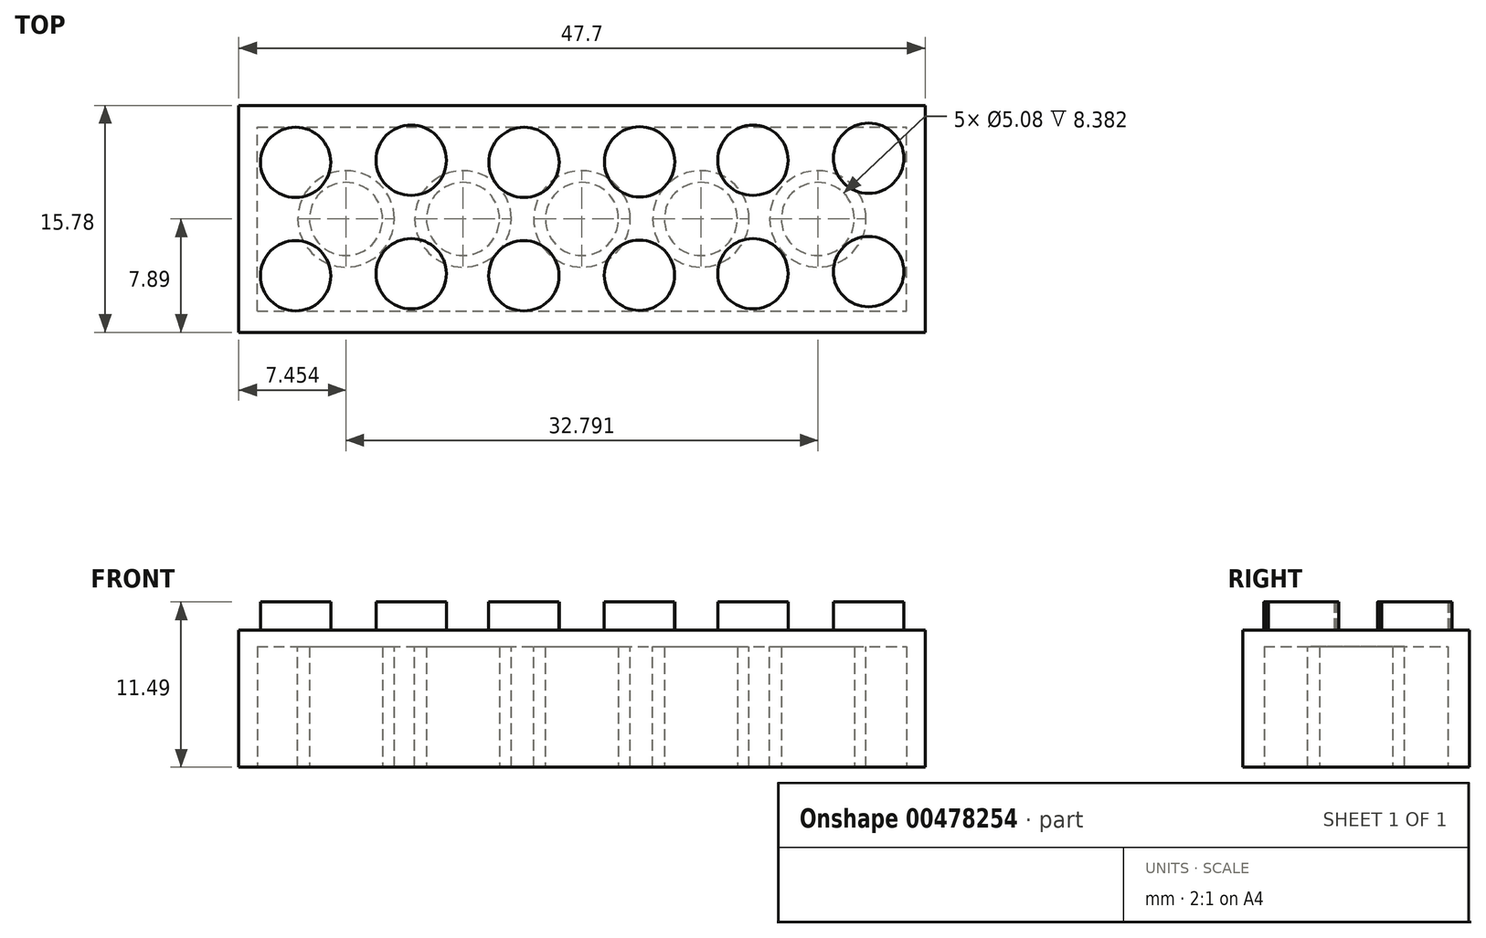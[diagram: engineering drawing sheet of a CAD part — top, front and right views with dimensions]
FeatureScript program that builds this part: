
annotation { "Feature Type Name" : "Feature", "Feature Type Description" : "" }
export const myFeature = defineFeature(function(context is Context, id is Id, definition is map)
    precondition{}
    {
        {
            var Q0;
            Q0=qCreatedBy(makeId("Top.planeOp"),FACE);
            var sketch = newSketch(context, id + "F0", { "sketchPlane" : qUnion([Q0])});
            skLineSegment(sketch, "E0.bottom", {"start": v(23.85, 7.89) * mm, "end": v(-23.85, 7.89) * mm});
            skLineSegment(sketch, "E0.top", {"start": v(23.85, -7.89) * mm, "end": v(-23.85, -7.89) * mm});
            skLineSegment(sketch, "E0.left", {"start": v(23.85, 7.89) * mm, "end": v(23.85, -7.89) * mm});
            skLineSegment(sketch, "E0.right", {"start": v(-23.85, 7.89) * mm, "end": v(-23.85, -7.89) * mm});
            skSolve(sketch);
        }
        {
            var Q0;
            Q0=makeQuery(id+"F0.imprint","IMPRINT",FACE,{"disambiguationData":[TD([[makeQuery(id+"F0.imprint","IMPRINT",EDGE,{"derivedFrom":sQuery(id+"F0.wireOp",EDGE,"E0.bottom")}),1.0]])]});
            extrude(context, id + "F1", {"entities" : qUnion([Q0]), "depth" : 9.52 * mm, "offsetDistance" : 25.4 * mm});
        }
        {
            var Q0;
            Q0=makeQuery(id+"F1.opExtrude","CAP_FACE",FACE,{"disambiguationData":[OSD([sQuery(id+"F0.wireOp",EDGE,"E0.bottom"),sQuery(id+"F0.wireOp",EDGE,"E0.top"),sQuery(id+"F0.wireOp",EDGE,"E0.left"),sQuery(id+"F0.wireOp",EDGE,"E0.right")])],"isStart":false});
            var sketch = newSketch(context, id + "F2", { "sketchPlane" : qUnion([Q0])});
            skPoint(sketch, "E1.middle", {"position": v(0, 0) * mm});
            skCircle(sketch, "E2", {"center": v(-19.9, 3.93) * mm, "radius": 2.44 * mm});
            skCircle(sketch, "E3", {"center": v(-11.87, 4.08) * mm, "radius": 2.44 * mm});
            skCircle(sketch, "E4", {"center": v(-19.9, -3.95) * mm, "radius": 2.44 * mm});
            skCircle(sketch, "E5", {"center": v(-11.87, -3.8) * mm, "radius": 2.44 * mm});
            skCircle(sketch, "E6", {"center": v(-4.03, 3.93) * mm, "radius": 2.44 * mm});
            skCircle(sketch, "E7", {"center": v(4.01, 3.97) * mm, "radius": 2.44 * mm});
            skCircle(sketch, "E8", {"center": v(-4.04, -3.95) * mm, "radius": 2.44 * mm});
            skCircle(sketch, "E9", {"center": v(4, -3.91) * mm, "radius": 2.44 * mm});
            skCircle(sketch, "E10", {"center": v(11.89, 4.08) * mm, "radius": 2.44 * mm});
            skCircle(sketch, "E11", {"center": v(19.92, 4.22) * mm, "radius": 2.44 * mm});
            skCircle(sketch, "E12", {"center": v(11.89, -3.8) * mm, "radius": 2.44 * mm});
            skCircle(sketch, "E13", {"center": v(19.92, -3.66) * mm, "radius": 2.44 * mm});
            skSolve(sketch);
        }
        {
            var Q0;
            Q0=makeQuery(id+"F2.imprint","IMPRINT",FACE,{"disambiguationData":[TD([[makeQuery(id+"F2.imprint","IMPRINT",EDGE,{"derivedFrom":sQuery(id+"F2.wireOp",EDGE,"E9")}),1.0]])]});
            var Q1;
            Q1=makeQuery(id+"F2.imprint","IMPRINT",FACE,{"disambiguationData":[TD([[makeQuery(id+"F2.imprint","IMPRINT",EDGE,{"derivedFrom":sQuery(id+"F2.wireOp",EDGE,"E8")}),1.0]])]});
            var Q2;
            Q2=makeQuery(id+"F2.imprint","IMPRINT",FACE,{"disambiguationData":[TD([[makeQuery(id+"F2.imprint","IMPRINT",EDGE,{"derivedFrom":sQuery(id+"F2.wireOp",EDGE,"E7")}),1.0]])]});
            var Q3;
            Q3=makeQuery(id+"F2.imprint","IMPRINT",FACE,{"disambiguationData":[TD([[makeQuery(id+"F2.imprint","IMPRINT",EDGE,{"derivedFrom":sQuery(id+"F2.wireOp",EDGE,"E12")}),1.0]])]});
            var Q4;
            Q4=makeQuery(id+"F2.imprint","IMPRINT",FACE,{"disambiguationData":[TD([[makeQuery(id+"F2.imprint","IMPRINT",EDGE,{"derivedFrom":sQuery(id+"F2.wireOp",EDGE,"E5")}),1.0]])]});
            var Q5;
            Q5=makeQuery(id+"F2.imprint","IMPRINT",FACE,{"disambiguationData":[TD([[makeQuery(id+"F2.imprint","IMPRINT",EDGE,{"derivedFrom":sQuery(id+"F2.wireOp",EDGE,"E6")}),1.0]])]});
            var Q6;
            Q6=makeQuery(id+"F2.imprint","IMPRINT",FACE,{"disambiguationData":[TD([[makeQuery(id+"F2.imprint","IMPRINT",EDGE,{"derivedFrom":sQuery(id+"F2.wireOp",EDGE,"E10")}),1.0]])]});
            var Q7;
            Q7=makeQuery(id+"F2.imprint","IMPRINT",FACE,{"disambiguationData":[TD([[makeQuery(id+"F2.imprint","IMPRINT",EDGE,{"derivedFrom":sQuery(id+"F2.wireOp",EDGE,"E3")}),1.0]])]});
            var Q8;
            Q8=makeQuery(id+"F2.imprint","IMPRINT",FACE,{"disambiguationData":[TD([[makeQuery(id+"F2.imprint","IMPRINT",EDGE,{"derivedFrom":sQuery(id+"F2.wireOp",EDGE,"E4")}),1.0]])]});
            var Q9;
            Q9=makeQuery(id+"F2.imprint","IMPRINT",FACE,{"disambiguationData":[TD([[makeQuery(id+"F2.imprint","IMPRINT",EDGE,{"derivedFrom":sQuery(id+"F2.wireOp",EDGE,"E13")}),1.0]])]});
            var Q10;
            Q10=makeQuery(id+"F2.imprint","IMPRINT",FACE,{"disambiguationData":[TD([[makeQuery(id+"F2.imprint","IMPRINT",EDGE,{"derivedFrom":sQuery(id+"F2.wireOp",EDGE,"E11")}),1.0]])]});
            var Q11;
            Q11=makeQuery(id+"F2.imprint","IMPRINT",FACE,{"disambiguationData":[TD([[makeQuery(id+"F2.imprint","IMPRINT",EDGE,{"derivedFrom":sQuery(id+"F2.wireOp",EDGE,"E2")}),1.0]])]});
            extrude(context, id + "F3", {"entities" : qUnion([Q0, Q1, Q2, Q3, Q4, Q5, Q6, Q7, Q8, Q9, Q10, Q11]), "operationType" : NewBodyOperationType.ADD, "depth" : 1.97 * mm, "offsetDistance" : 25.4 * mm});
        }
        {
            var Q0;
            Q0=makeQuery(id+"F1.opExtrude","CAP_FACE",FACE,{"disambiguationData":[OSD([sQuery(id+"F0.wireOp",EDGE,"E0.bottom"),sQuery(id+"F0.wireOp",EDGE,"E0.top"),sQuery(id+"F0.wireOp",EDGE,"E0.left"),sQuery(id+"F0.wireOp",EDGE,"E0.right")])],"isStart":true});
            var sketch = newSketch(context, id + "F4", { "sketchPlane" : qUnion([Q0])});
            skLineSegment(sketch, "E14.bottom", {"start": v(-22.57, 6.39) * mm, "end": v(22.57, 6.39) * mm});
            skLineSegment(sketch, "E14.top", {"start": v(-22.57, -6.39) * mm, "end": v(22.57, -6.39) * mm});
            skLineSegment(sketch, "E14.left", {"start": v(-22.57, 6.39) * mm, "end": v(-22.57, -6.39) * mm});
            skLineSegment(sketch, "E14.right", {"start": v(22.57, 6.39) * mm, "end": v(22.57, -6.39) * mm});
            skPoint(sketch, "E14.middle", {"position": v(0, 0) * mm});
            skSolve(sketch);
        }
        {
            var Q0;
            Q0=makeQuery(id+"F4.imprint","IMPRINT",FACE,{"disambiguationData":[TD([[makeQuery(id+"F4.imprint","IMPRINT",EDGE,{"derivedFrom":sQuery(id+"F4.wireOp",EDGE,"E14.bottom")}),-1.0]])]});
            extrude(context, id + "F5", {"entities" : qUnion([Q0]), "operationType" : NewBodyOperationType.REMOVE, "oppositeDirection" : true, "depth" : 8.38 * mm, "offsetDistance" : 25.4 * mm});
        }
        {
            var Q0;
            Q0=makeQuery(id+"F5.boolean.opBoolean","COPY",FACE,{"derivedFrom":makeQuery(id+"F5.opExtrude","CAP_FACE",FACE,{"disambiguationData":[OSD([sQuery(id+"F4.wireOp",EDGE,"E14.bottom"),sQuery(id+"F4.wireOp",EDGE,"E14.top"),sQuery(id+"F4.wireOp",EDGE,"E14.left"),sQuery(id+"F4.wireOp",EDGE,"E14.right")])],"isStart":false})});
            var sketch = newSketch(context, id + "F6", { "sketchPlane" : qUnion([Q0])});
            skCircle(sketch, "E15", {"center": v(0, 0) * mm, "radius": 3.35 * mm});
            skCircle(sketch, "E16", {"center": v(-16.4, 0) * mm, "radius": 3.35 * mm});
            skCircle(sketch, "E17", {"center": v(-8.27, 0) * mm, "radius": 3.35 * mm});
            skCircle(sketch, "E18", {"center": v(8.27, 0) * mm, "radius": 3.35 * mm});
            skCircle(sketch, "E19", {"center": v(16.4, 0) * mm, "radius": 3.35 * mm});
            skSolve(sketch);
        }
        {
            var Q0;
            Q0=makeQuery(id+"F6.imprint","IMPRINT",FACE,{"disambiguationData":[TD([[makeQuery(id+"F6.imprint","IMPRINT",EDGE,{"derivedFrom":sQuery(id+"F6.wireOp",EDGE,"E15")}),1.0]])]});
            var Q1;
            Q1=makeQuery(id+"F6.imprint","IMPRINT",FACE,{"disambiguationData":[TD([[makeQuery(id+"F6.imprint","IMPRINT",EDGE,{"derivedFrom":sQuery(id+"F6.wireOp",EDGE,"E16")}),1.0]])]});
            var Q2;
            Q2=makeQuery(id+"F6.imprint","IMPRINT",FACE,{"disambiguationData":[TD([[makeQuery(id+"F6.imprint","IMPRINT",EDGE,{"derivedFrom":sQuery(id+"F6.wireOp",EDGE,"E17")}),1.0]])]});
            var Q3;
            Q3=makeQuery(id+"F6.imprint","IMPRINT",FACE,{"disambiguationData":[TD([[makeQuery(id+"F6.imprint","IMPRINT",EDGE,{"derivedFrom":sQuery(id+"F6.wireOp",EDGE,"E18")}),1.0]])]});
            var Q4;
            Q4=makeQuery(id+"F6.imprint","IMPRINT",FACE,{"disambiguationData":[TD([[makeQuery(id+"F6.imprint","IMPRINT",EDGE,{"derivedFrom":sQuery(id+"F6.wireOp",EDGE,"E19")}),1.0]])]});
            extrude(context, id + "F7", {"entities" : qUnion([Q0, Q1, Q2, Q3, Q4]), "operationType" : NewBodyOperationType.ADD, "depth" : 8.38 * mm, "offsetDistance" : 25.4 * mm});
        }
        {
            var Q0;
            Q0=makeQuery(id+"F7.opExtrude","CAP_FACE",FACE,{"disambiguationData":[OSD([sQuery(id+"F6.wireOp",EDGE,"E15")])],"isStart":false});
            var sketch = newSketch(context, id + "F8", { "sketchPlane" : qUnion([Q0])});
            skCircle(sketch, "E20", {"center": v(-16.4, 0) * mm, "radius": 2.54 * mm});
            skCircle(sketch, "E21", {"center": v(-8.27, 0) * mm, "radius": 2.54 * mm});
            skCircle(sketch, "E22", {"center": v(0, 0) * mm, "radius": 2.54 * mm});
            skCircle(sketch, "E23", {"center": v(8.27, 0) * mm, "radius": 2.54 * mm});
            skCircle(sketch, "E24", {"center": v(16.4, 0) * mm, "radius": 2.54 * mm});
            skSolve(sketch);
        }
        {
            var Q0;
            Q0=makeQuery(id+"F8.imprint","IMPRINT",FACE,{"disambiguationData":[TD([[makeQuery(id+"F8.imprint","IMPRINT",EDGE,{"derivedFrom":sQuery(id+"F8.wireOp",EDGE,"E20")}),1.0]])]});
            var Q1;
            Q1=makeQuery(id+"F8.imprint","IMPRINT",FACE,{"disambiguationData":[TD([[makeQuery(id+"F8.imprint","IMPRINT",EDGE,{"derivedFrom":sQuery(id+"F8.wireOp",EDGE,"E21")}),1.0]])]});
            var Q2;
            Q2=makeQuery(id+"F8.imprint","IMPRINT",FACE,{"disambiguationData":[TD([[makeQuery(id+"F8.imprint","IMPRINT",EDGE,{"derivedFrom":sQuery(id+"F8.wireOp",EDGE,"E22")}),1.0]])]});
            var Q3;
            Q3=makeQuery(id+"F8.imprint","IMPRINT",FACE,{"disambiguationData":[TD([[makeQuery(id+"F8.imprint","IMPRINT",EDGE,{"derivedFrom":sQuery(id+"F8.wireOp",EDGE,"E23")}),1.0]])]});
            var Q4;
            Q4=makeQuery(id+"F8.imprint","IMPRINT",FACE,{"disambiguationData":[TD([[makeQuery(id+"F8.imprint","IMPRINT",EDGE,{"derivedFrom":sQuery(id+"F8.wireOp",EDGE,"E24")}),1.0]])]});
            extrude(context, id + "F9", {"entities" : qUnion([Q0, Q1, Q2, Q3, Q4]), "operationType" : NewBodyOperationType.REMOVE, "oppositeDirection" : true, "depth" : 8.38 * mm, "offsetDistance" : 25.4 * mm});
        }
    });
